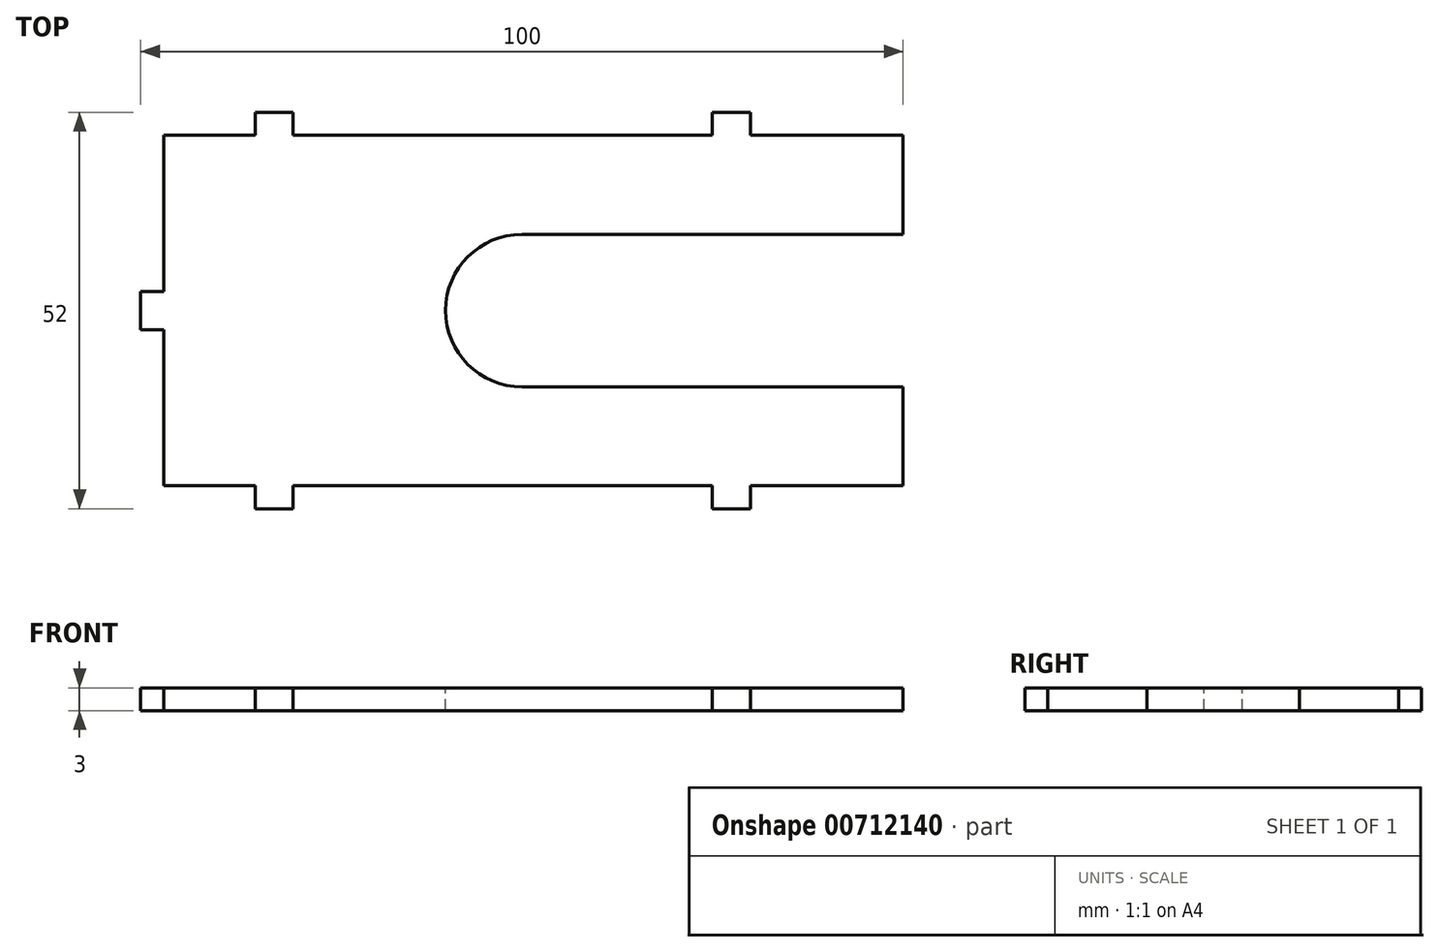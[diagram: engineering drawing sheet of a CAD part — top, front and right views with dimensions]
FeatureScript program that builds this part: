
annotation { "Feature Type Name" : "Feature", "Feature Type Description" : "" }
export const myFeature = defineFeature(function(context is Context, id is Id, definition is map)
    precondition{}
    {
        {
            var Q0;
            Q0=qCreatedBy(makeId("Top.planeOp"),FACE);
            var sketch = newSketch(context, id + "F0", { "sketchPlane" : qUnion([Q0])});
            skLineSegment(sketch, "E0.bottom", {"start": v(50, -26) * mm, "end": v(-50, -26) * mm});
            skLineSegment(sketch, "E0.top", {"start": v(50, 26) * mm, "end": v(-50, 26) * mm});
            skLineSegment(sketch, "E0.left", {"start": v(50, -26) * mm, "end": v(50, 26) * mm});
            skLineSegment(sketch, "E0.right", {"start": v(-50, -26) * mm, "end": v(-50, 26) * mm});
            skPoint(sketch, "E0.middle", {"position": v(0, 0) * mm});
            skSolve(sketch);
        }
        {
            var Q0;
            Q0 = qSketchRegion(id + "F0", true);
            extrude(context, id + "F1", {"entities" : qUnion([Q0]), "depth" : 3 * mm, "offsetDistance" : 25 * mm});
        }
        {
            var Q0;
            Q0=qCreatedBy(makeId("Top.planeOp"),FACE);
            var sketch = newSketch(context, id + "F2", { "sketchPlane" : qUnion([Q0])});
            skPoint(sketch, "E1", {"position": v(-30, 26) * mm});
            skPoint(sketch, "E2", {"position": v(30, 26) * mm});
            skPoint(sketch, "E3", {"position": v(-30, -26) * mm});
            skPoint(sketch, "E4", {"position": v(30, -26) * mm});
            skPoint(sketch, "E5", {"position": v(-50, 0) * mm});
            skSolve(sketch);
        }
        {
            var Q0;
            Q0=makeQuery(id+"F1.opExtrude","CAP_FACE",FACE,{"disambiguationData":[OSD([sQuery(id+"F0.wireOp",EDGE,"E0.bottom"),sQuery(id+"F0.wireOp",EDGE,"E0.top"),sQuery(id+"F0.wireOp",EDGE,"E0.left"),sQuery(id+"F0.wireOp",EDGE,"E0.right")])],"isStart":false});
            var sketch = newSketch(context, id + "F3", { "sketchPlane" : qUnion([Q0])});
            skLineSegment(sketch, "E6", {"start": v(-50, 23) * mm, "end": v(50, 23) * mm});
            skLineSegment(sketch, "E7", {"start": v(-50, -23) * mm, "end": v(50, -23) * mm});
            skLineSegment(sketch, "E8", {"start": v(-47, 26) * mm, "end": v(-47, -26) * mm});
            skLineSegment(sketch, "E9", {"start": v(47, 26) * mm, "end": v(47, -26) * mm});
            skPoint(sketch, "E10", {"position": v(-35, 26) * mm});
            skPoint(sketch, "E11", {"position": v(25, 26) * mm});
            skPoint(sketch, "E12", {"position": v(25, -26) * mm});
            skPoint(sketch, "E13", {"position": v(-35, -26) * mm});
            skPoint(sketch, "E14", {"position": v(-50, -2.5) * mm});
            skPoint(sketch, "E15", {"position": v(-50, 2.5) * mm});
            skLineSegment(sketch, "E16", {"start": v(-35, 26) * mm, "end": v(-35, 23) * mm});
            skLineSegment(sketch, "E17", {"start": v(-30, 26) * mm, "end": v(-30, 23) * mm});
            skLineSegment(sketch, "E18", {"start": v(25, 26) * mm, "end": v(25, 23) * mm});
            skLineSegment(sketch, "E19", {"start": v(30, 26) * mm, "end": v(30, 23) * mm});
            skLineSegment(sketch, "E20", {"start": v(-50, 2.5) * mm, "end": v(-47, 2.5) * mm});
            skLineSegment(sketch, "E21", {"start": v(-50, -2.5) * mm, "end": v(-47, -2.5) * mm});
            skLineSegment(sketch, "E22", {"start": v(-35, -26) * mm, "end": v(-35, -23) * mm});
            skLineSegment(sketch, "E23", {"start": v(-30, -26) * mm, "end": v(-30, -23) * mm});
            skLineSegment(sketch, "E24", {"start": v(25, -26) * mm, "end": v(25, -23) * mm});
            skLineSegment(sketch, "E25", {"start": v(30, -26) * mm, "end": v(30, -23) * mm});
            skSolve(sketch);
        }
        {
            var Q0;
            {var subQ0=sQuery(id+"F3.wireOp",EDGE,"E16");Q0=makeQuery(id+"F3.imprint","IMPRINT",FACE,{"disambiguationData":[TD([[makeQuery(id+"F3.imprint","IMPRINT",EDGE,{"derivedFrom":subQ0}),-1.0]])]});}
            var Q1;
            {var subQ0=sQuery(id+"F3.wireOp",EDGE,"E6");var subQ1=makeQuery(id+"F1.opExtrude","CAP_EDGE",EDGE,{"disambiguationData":[OSD([sQuery(id+"F0.wireOp",EDGE,"E0.right")])],"isStart":false});var subQ2=makeQuery(id+"F3.imprint","INTERSECT",VERTEX,{"derivedFrom":[subQ1,subQ0]});Q1=makeQuery(id+"F3.imprint","IMPRINT",FACE,{"disambiguationData":[TD([[makeQuery(id+"F3.imprint","IMPRINT",EDGE,{"disambiguationData":[TD([[subQ2,-1.0]])],"derivedFrom":subQ0}),1.0]])]});}
            var Q2;
            {var subQ5=sQuery(id+"F3.wireOp",EDGE,"E20");Q2=makeQuery(id+"F3.imprint","IMPRINT",FACE,{"disambiguationData":[TD([[makeQuery(id+"F3.imprint","IMPRINT",EDGE,{"derivedFrom":subQ5}),1.0]])]});}
            var Q3;
            {var subQ5=sQuery(id+"F3.wireOp",EDGE,"E21");Q3=makeQuery(id+"F3.imprint","IMPRINT",FACE,{"disambiguationData":[TD([[makeQuery(id+"F3.imprint","IMPRINT",EDGE,{"derivedFrom":subQ5}),-1.0]])]});}
            var Q4;
            {var subQ0=sQuery(id+"F3.wireOp",EDGE,"E7");var subQ1=makeQuery(id+"F1.opExtrude","CAP_EDGE",EDGE,{"disambiguationData":[OSD([sQuery(id+"F0.wireOp",EDGE,"E0.right")])],"isStart":false});var subQ2=makeQuery(id+"F3.imprint","INTERSECT",VERTEX,{"derivedFrom":[subQ1,subQ0]});Q4=makeQuery(id+"F3.imprint","IMPRINT",FACE,{"disambiguationData":[TD([[makeQuery(id+"F3.imprint","IMPRINT",EDGE,{"disambiguationData":[TD([[subQ2,-1.0]])],"derivedFrom":subQ0}),-1.0]])]});}
            var Q5;
            {var subQ0=sQuery(id+"F3.wireOp",EDGE,"E22");Q5=makeQuery(id+"F3.imprint","IMPRINT",FACE,{"disambiguationData":[TD([[makeQuery(id+"F3.imprint","IMPRINT",EDGE,{"derivedFrom":subQ0}),1.0]])]});}
            var Q6;
            {var subQ0=sQuery(id+"F3.wireOp",EDGE,"E23");Q6=makeQuery(id+"F3.imprint","IMPRINT",FACE,{"disambiguationData":[TD([[makeQuery(id+"F3.imprint","IMPRINT",EDGE,{"derivedFrom":subQ0}),-1.0]])]});}
            var Q7;
            {var subQ0=sQuery(id+"F3.wireOp",EDGE,"E25");Q7=makeQuery(id+"F3.imprint","IMPRINT",FACE,{"disambiguationData":[TD([[makeQuery(id+"F3.imprint","IMPRINT",EDGE,{"derivedFrom":subQ0}),-1.0]])]});}
            var Q8;
            {var subQ0=sQuery(id+"F3.wireOp",EDGE,"E7");var subQ1=makeQuery(id+"F1.opExtrude","CAP_EDGE",EDGE,{"disambiguationData":[OSD([sQuery(id+"F0.wireOp",EDGE,"E0.left")])],"isStart":false});var subQ2=makeQuery(id+"F3.imprint","INTERSECT",VERTEX,{"derivedFrom":[subQ1,subQ0]});Q8=makeQuery(id+"F3.imprint","IMPRINT",FACE,{"disambiguationData":[TD([[makeQuery(id+"F3.imprint","IMPRINT",EDGE,{"disambiguationData":[TD([[subQ2,1.0]])],"derivedFrom":subQ0}),-1.0]])]});}
            var Q9;
            {var subQ0=sQuery(id+"F3.wireOp",EDGE,"E6");var subQ1=makeQuery(id+"F1.opExtrude","CAP_EDGE",EDGE,{"disambiguationData":[OSD([sQuery(id+"F0.wireOp",EDGE,"E0.left")])],"isStart":false});var subQ2=makeQuery(id+"F3.imprint","INTERSECT",VERTEX,{"derivedFrom":[subQ1,subQ0]});Q9=makeQuery(id+"F3.imprint","IMPRINT",FACE,{"disambiguationData":[TD([[makeQuery(id+"F3.imprint","IMPRINT",EDGE,{"disambiguationData":[TD([[subQ2,1.0]])],"derivedFrom":subQ0}),1.0]])]});}
            var Q10;
            {var subQ0=sQuery(id+"F3.wireOp",EDGE,"E19");Q10=makeQuery(id+"F3.imprint","IMPRINT",FACE,{"disambiguationData":[TD([[makeQuery(id+"F3.imprint","IMPRINT",EDGE,{"derivedFrom":subQ0}),1.0]])]});}
            var Q11;
            {var subQ0=sQuery(id+"F3.wireOp",EDGE,"E17");Q11=makeQuery(id+"F3.imprint","IMPRINT",FACE,{"disambiguationData":[TD([[makeQuery(id+"F3.imprint","IMPRINT",EDGE,{"derivedFrom":subQ0}),1.0]])]});}
            extrude(context, id + "F4", {"entities" : qUnion([Q0, Q1, Q2, Q3, Q4, Q5, Q6, Q7, Q8, Q9, Q10, Q11]), "operationType" : NewBodyOperationType.REMOVE, "endBound" : BoundingType.THROUGH_ALL, "oppositeDirection" : true, "depth" : 25 * mm, "offsetDistance" : 25 * mm});
        }
        {
            var Q0;
            Q0=makeQuery(id+"F1.opExtrude","CAP_FACE",FACE,{"disambiguationData":[OSD([sQuery(id+"F0.wireOp",EDGE,"E0.bottom"),sQuery(id+"F0.wireOp",EDGE,"E0.top"),sQuery(id+"F0.wireOp",EDGE,"E0.left"),sQuery(id+"F0.wireOp",EDGE,"E0.right")])],"isStart":false});
            var sketch = newSketch(context, id + "F5", { "sketchPlane" : qUnion([Q0])});
            skCircle(sketch, "E26", {"center": v(0, 0) * mm, "radius": 10 * mm});
            skLineSegment(sketch, "E27", {"start": v(0, 10) * mm, "end": v(50, 10) * mm});
            skLineSegment(sketch, "E28", {"start": v(0, -10) * mm, "end": v(50, -10) * mm});
            skSolve(sketch);
        }
        {
            var Q0;
            Q0 = qSketchRegion(id + "F5", true);
            var Q1;
            {var subQ0=sQuery(id+"F5.wireOp",EDGE,"E27");Q1=makeQuery(id+"F5.imprint","IMPRINT",FACE,{"disambiguationData":[TD([[makeQuery(id+"F5.imprint","IMPRINT",EDGE,{"derivedFrom":subQ0}),-1.0]])]});}
            extrude(context, id + "F6", {"entities" : qUnion([Q0, Q1]), "operationType" : NewBodyOperationType.REMOVE, "endBound" : BoundingType.THROUGH_ALL, "oppositeDirection" : true, "depth" : 25 * mm, "offsetDistance" : 25 * mm});
        }
    });
